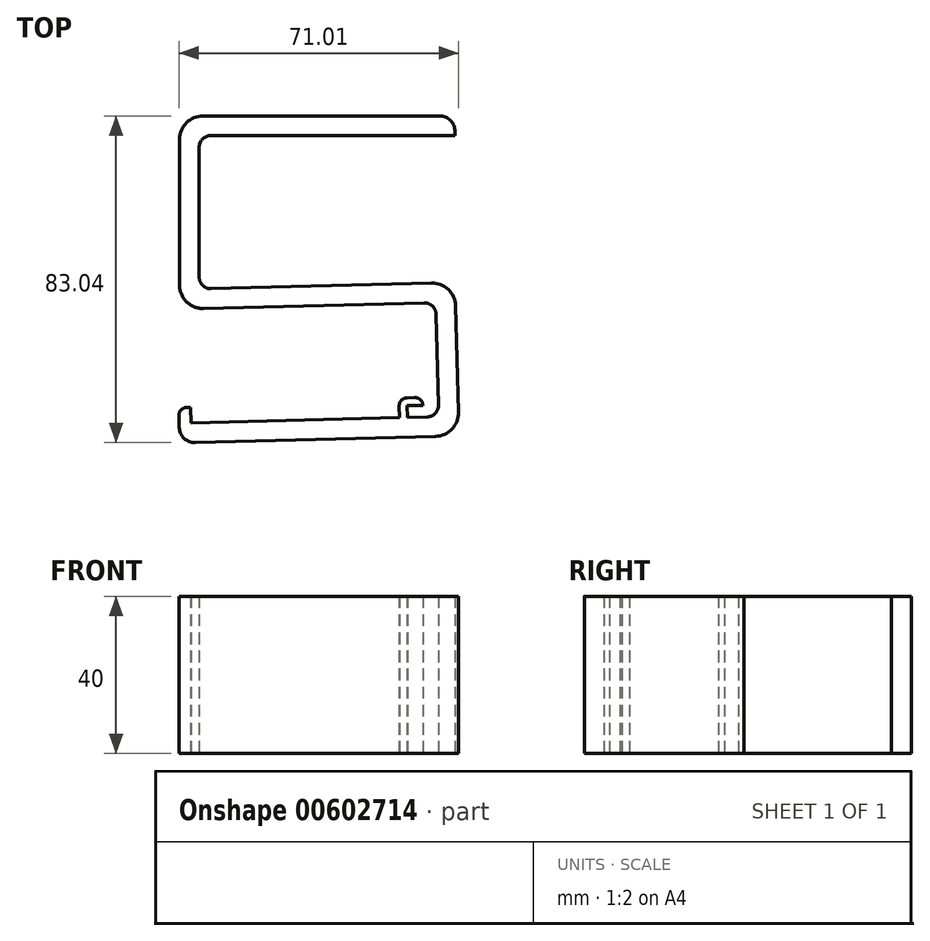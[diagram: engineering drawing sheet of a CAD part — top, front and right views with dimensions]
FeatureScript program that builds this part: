
annotation { "Feature Type Name" : "Feature", "Feature Type Description" : "" }
export const myFeature = defineFeature(function(context is Context, id is Id, definition is map)
    precondition{}
    {
        {
            var Q0;
            Q0=qCreatedBy(makeId("Top.planeOp"),FACE);
            var sketch = newSketch(context, id + "F0", { "sketchPlane" : qUnion([Q0])});
            skLineSegment(sketch, "E0", {"start": v(6, 0) * mm, "end": v(66, 0) * mm});
            skLineSegment(sketch, "E1", {"start": v(70, -4) * mm, "end": v(70, -5) * mm});
            skLineSegment(sketch, "E2", {"start": v(70, -5) * mm, "end": v(8, -5) * mm});
            skLineSegment(sketch, "E3", {"start": v(5, -8) * mm, "end": v(5, -40.92) * mm});
            skLineSegment(sketch, "E4", {"start": v(8.08, -43.92) * mm, "end": v(64, -42.45) * mm});
            skLineSegment(sketch, "E5", {"start": v(70.16, -48.3) * mm, "end": v(70.86, -75.29) * mm});
            skLineSegment(sketch, "E6", {"start": v(65.02, -81.44) * mm, "end": v(4.04, -83.04) * mm});
            skLineSegment(sketch, "E7", {"start": v(-0.06, -79.14) * mm, "end": v(-0.14, -76.15) * mm});
            skLineSegment(sketch, "E8", {"start": v(1.8, -74.1) * mm, "end": v(2.8, -74.07) * mm});
            skLineSegment(sketch, "E9", {"start": v(2.8, -74.07) * mm, "end": v(2.91, -78.07) * mm});
            skLineSegment(sketch, "E10", {"start": v(2.91, -78.07) * mm, "end": v(55.9, -76.68) * mm});
            skLineSegment(sketch, "E11", {"start": v(55.9, -76.68) * mm, "end": v(55.82, -73.68) * mm});
            skLineSegment(sketch, "E12", {"start": v(57.76, -71.63) * mm, "end": v(59.76, -71.58) * mm});
            skLineSegment(sketch, "E13", {"start": v(61.81, -73.52) * mm, "end": v(61.81, -73.52) * mm});
            skLineSegment(sketch, "E14", {"start": v(61.81, -73.52) * mm, "end": v(57.82, -73.63) * mm});
            skLineSegment(sketch, "E15", {"start": v(62.13, -47.5) * mm, "end": v(6.16, -48.97) * mm});
            skLineSegment(sketch, "E16", {"start": v(0, -42.97) * mm, "end": v(0, -6) * mm});
            skLineSegment(sketch, "E17", {"start": v(65.21, -50.43) * mm, "end": v(65.81, -73.42) * mm});
            skLineSegment(sketch, "E18", {"start": v(62.9, -76.5) * mm, "end": v(57.9, -76.63) * mm});
            skLineSegment(sketch, "E19", {"start": v(57.9, -76.63) * mm, "end": v(57.82, -73.63) * mm});
            skPoint(sketch, "E20.visualSharp", {"position": v(-0.2, -74.15) * mm});
            skArc(sketch, "E20.filletArc", {"start": v(1.8, -74.1) * mm, "mid": v(0.41, -74.72) * mm, "end": v(-0.14, -76.15) * mm});
            skPoint(sketch, "E21.visualSharp", {"position": v(5, -5) * mm});
            skArc(sketch, "E21.filletArc", {"start": v(8, -5) * mm, "mid": v(5.88, -5.88) * mm, "end": v(5, -8) * mm});
            skPoint(sketch, "E22.visualSharp", {"position": v(5, -44) * mm});
            skArc(sketch, "E22.filletArc", {"start": v(5, -40.92) * mm, "mid": v(5.9, -43.07) * mm, "end": v(8.08, -43.92) * mm});
            skPoint(sketch, "E23.visualSharp", {"position": v(65.13, -47.43) * mm});
            skArc(sketch, "E23.filletArc", {"start": v(65.21, -50.43) * mm, "mid": v(64.28, -48.33) * mm, "end": v(62.13, -47.5) * mm});
            skPoint(sketch, "E24.visualSharp", {"position": v(65.9, -76.42) * mm});
            skArc(sketch, "E24.filletArc", {"start": v(62.9, -76.5) * mm, "mid": v(65, -75.56) * mm, "end": v(65.81, -73.42) * mm});
            skPoint(sketch, "E25.visualSharp", {"position": v(71.02, -81.28) * mm});
            skArc(sketch, "E25.filletArc", {"start": v(65.02, -81.44) * mm, "mid": v(69.22, -79.57) * mm, "end": v(70.86, -75.29) * mm});
            skPoint(sketch, "E26.visualSharp", {"position": v(70, -42.3) * mm});
            skArc(sketch, "E26.filletArc", {"start": v(70.16, -48.3) * mm, "mid": v(68.29, -44.1) * mm, "end": v(64, -42.45) * mm});
            skPoint(sketch, "E27.visualSharp", {"position": v(0, 0) * mm});
            skArc(sketch, "E27.filletArc", {"start": v(6, 0) * mm, "mid": v(1.76, -1.76) * mm, "end": v(0, -6) * mm});
            skPoint(sketch, "E28.visualSharp", {"position": v(0, -49.13) * mm});
            skArc(sketch, "E28.filletArc", {"start": v(0, -42.97) * mm, "mid": v(1.81, -47.27) * mm, "end": v(6.16, -48.97) * mm});
            skPoint(sketch, "E29.visualSharp", {"position": v(0.05, -83.14) * mm});
            skArc(sketch, "E29.filletArc", {"start": v(-0.06, -79.14) * mm, "mid": v(1.19, -81.94) * mm, "end": v(4.04, -83.04) * mm});
            skPoint(sketch, "E30.visualSharp", {"position": v(70, 0) * mm});
            skArc(sketch, "E30.filletArc", {"start": v(70, -4) * mm, "mid": v(68.83, -1.17) * mm, "end": v(66, 0) * mm});
            skPoint(sketch, "E31.visualSharp", {"position": v(55.76, -71.68) * mm});
            skArc(sketch, "E31.filletArc", {"start": v(57.76, -71.63) * mm, "mid": v(56.37, -72.25) * mm, "end": v(55.82, -73.68) * mm});
            skPoint(sketch, "E32.visualSharp", {"position": v(61.76, -71.52) * mm});
            skArc(sketch, "E32.filletArc", {"start": v(61.81, -73.52) * mm, "mid": v(61.2, -72.12) * mm, "end": v(59.76, -71.58) * mm});
            skSolve(sketch);
        }
        {
            var Q0;
            Q0 = qSketchRegion(id + "F0", true);
            extrude(context, id + "F1", {"entities" : qUnion([Q0]), "depth" : 40 * mm, "offsetDistance" : 25 * mm});
        }
    });
